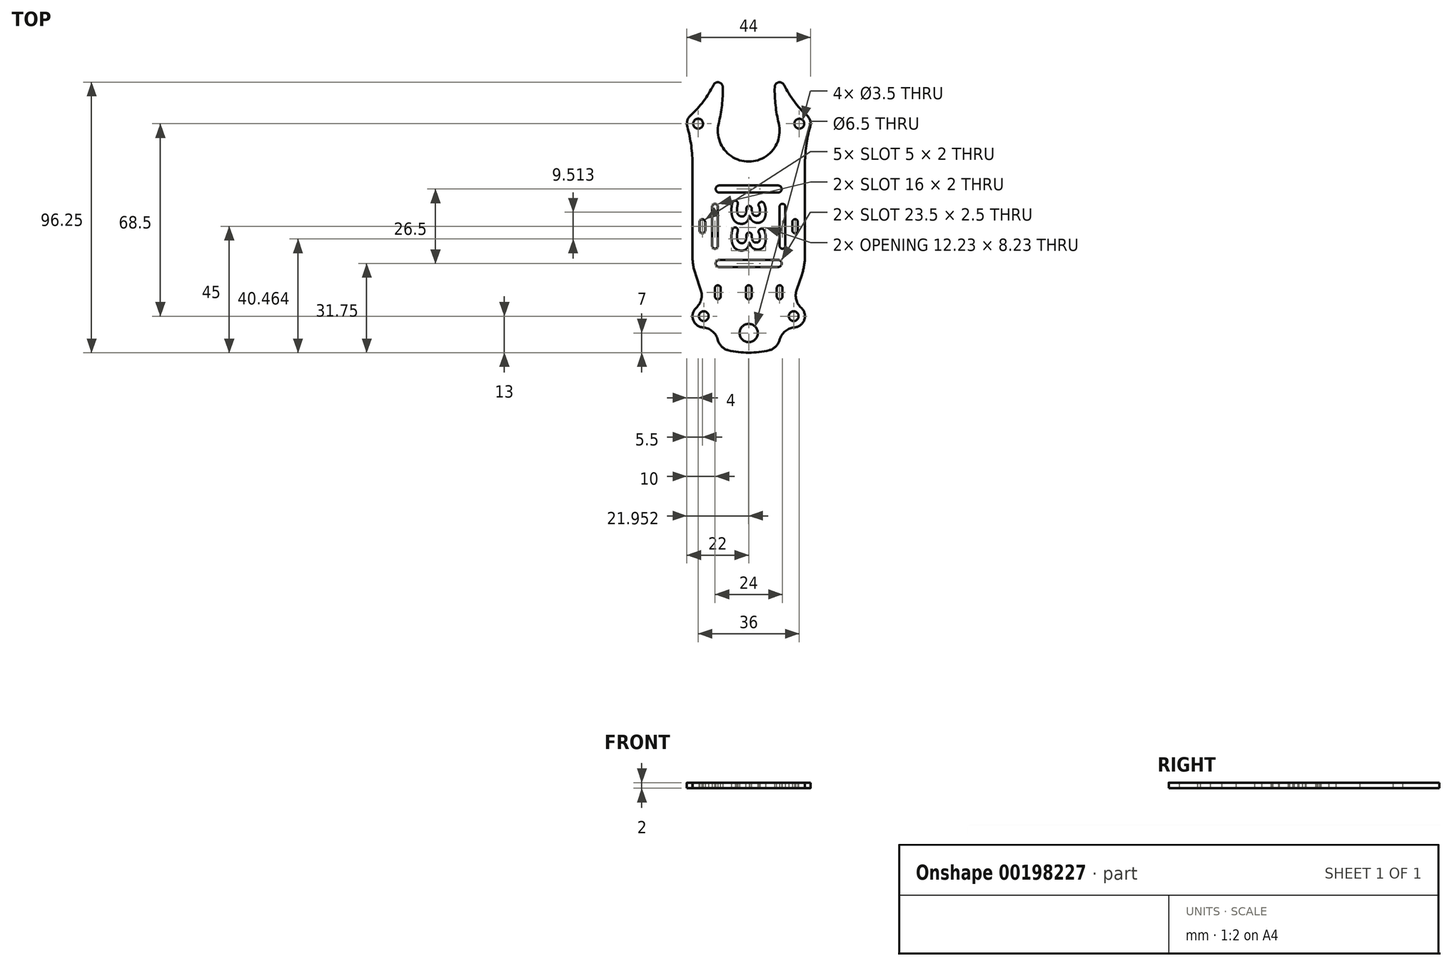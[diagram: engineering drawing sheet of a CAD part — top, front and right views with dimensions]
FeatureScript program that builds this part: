
annotation { "Feature Type Name" : "Feature", "Feature Type Description" : "" }
export const myFeature = defineFeature(function(context is Context, id is Id, definition is map)
    precondition{}
    {
        {
            var Q0;
            Q0=qCreatedBy(makeId("Top.planeOp"),FACE);
            var sketch = newSketch(context, id + "F0", { "sketchPlane" : qUnion([Q0])});
            skArc(sketch, "E0", {"start": v(-20.7, 39.46) * mm, "mid": v(-21.84, 37.62) * mm, "end": v(-21.86, 35.44) * mm});
            skLineSegment(sketch, "E1", {"start": v(-18.93, -17.14) * mm, "end": v(-17.05, -22.66) * mm});
            skArc(sketch, "E2", {"start": v(-10.68, 36.62) * mm, "mid": v(-8.66, 27.21) * mm, "end": v(0, 23) * mm});
            skLineSegment(sketch, "E3", {"start": v(0, 23) * mm, "end": v(0, -60) * mm, "construction": true});
            skCircle(sketch, "E4", {"center": v(-16, -32) * mm, "radius": 1.75 * mm});
            skArc(sketch, "E5.MirrorCS", {"start": v(10.68, 36.62) * mm, "mid": v(8.66, 27.21) * mm, "end": v(0, 23) * mm});
            skArc(sketch, "E6.MirrorCS", {"start": v(20.7, 39.46) * mm, "mid": v(21.84, 37.62) * mm, "end": v(21.86, 35.44) * mm});
            skCircle(sketch, "E7.MirrorC", {"center": v(16, -32) * mm, "radius": 1.75 * mm});
            skLineSegment(sketch, "E8.MirrorCS", {"start": v(18.93, -17.14) * mm, "end": v(17.05, -22.66) * mm});
            skCircle(sketch, "E9", {"center": v(-18, 36.5) * mm, "radius": 1.75 * mm});
            skCircle(sketch, "E10.MirrorC", {"center": v(18, 36.5) * mm, "radius": 1.75 * mm});
            skCircle(sketch, "E11", {"center": v(0, -38) * mm, "radius": 3.25 * mm});
            skArc(sketch, "E12", {"start": v(-7.28, -44.13) * mm, "mid": v(-3.66, -44.78) * mm, "end": v(0, -45) * mm});
            skLineSegment(sketch, "E13.trimOffspring", {"start": v(-20, 21.67) * mm, "end": v(-20, -10.69) * mm});
            skArc(sketch, "E14", {"start": v(16.32, -35.99) * mm, "mid": v(19.79, -33.3) * mm, "end": v(18.7, -29.04) * mm});
            skArc(sketch, "E15.filletArc", {"start": v(16.32, -35.99) * mm, "mid": v(13.12, -37.23) * mm, "end": v(11.13, -40.03) * mm});
            skArc(sketch, "E16.filletArc", {"start": v(17.05, -22.66) * mm, "mid": v(16.92, -26.1) * mm, "end": v(18.7, -29.04) * mm});
            skArc(sketch, "E17.MirrorCS", {"start": v(-16.32, -35.99) * mm, "mid": v(-13.12, -37.23) * mm, "end": v(-11.13, -40.03) * mm});
            skArc(sketch, "E18.MirrorCS", {"start": v(-16.32, -35.99) * mm, "mid": v(-19.79, -33.3) * mm, "end": v(-18.7, -29.04) * mm});
            skArc(sketch, "E19.MirrorCS", {"start": v(-17.05, -22.66) * mm, "mid": v(-16.92, -26.1) * mm, "end": v(-18.7, -29.04) * mm});
            skText(sketch, "E20", { "text": "33", "fontName": "OpenSans-Bold.ttf"});
            skLineSegment(sketch, "E21", {"start": v(-11.13, -40.03) * mm, "end": v(-10.84, -40.89) * mm});
            skLineSegment(sketch, "E22", {"start": v(11.13, -40.03) * mm, "end": v(10.84, -40.89) * mm});
            skLineSegment(sketch, "E23", {"start": v(-17.05, -22.66) * mm, "end": v(-11.13, -40.03) * mm, "construction": true});
            skLineSegment(sketch, "E24", {"start": v(17.05, -22.66) * mm, "end": v(11.13, -40.03) * mm, "construction": true});
            skArc(sketch, "E25", {"start": v(-9.25, 49.53) * mm, "mid": v(-10.62, 51.2) * mm, "end": v(-12.57, 50.27) * mm});
            skArc(sketch, "E26", {"start": v(-20.7, 39.46) * mm, "mid": v(-16.12, 44.48) * mm, "end": v(-12.57, 50.27) * mm});
            skArc(sketch, "E27.MirrorCS", {"start": v(9.25, 49.53) * mm, "mid": v(10.62, 51.2) * mm, "end": v(12.57, 50.27) * mm});
            skArc(sketch, "E28.MirrorCS", {"start": v(20.7, 39.46) * mm, "mid": v(16.12, 44.48) * mm, "end": v(12.57, 50.27) * mm});
            skPoint(sketch, "E29.visualSharp", {"position": v(-10, -43.34) * mm});
            skArc(sketch, "E29.filletArc", {"start": v(-10.84, -40.89) * mm, "mid": v(-9.47, -42.97) * mm, "end": v(-7.28, -44.13) * mm});
            skPoint(sketch, "E30.visualSharp", {"position": v(10, -43.34) * mm});
            skArc(sketch, "E30.filletArc", {"start": v(7.28, -44.13) * mm, "mid": v(9.47, -42.97) * mm, "end": v(10.84, -40.89) * mm});
            skLineSegment(sketch, "E31", {"start": v(-16.5, 1.5) * mm, "end": v(-16.5, -1.5) * mm, "construction": true});
            skArc(sketch, "E32.0.startCap", {"start": v(-17.5, 1.5) * mm, "mid": v(-16.5, 2.5) * mm, "end": v(-15.5, 1.5) * mm});
            skArc(sketch, "E32.0.endCap", {"start": v(-15.5, -1.5) * mm, "mid": v(-16.5, -2.5) * mm, "end": v(-17.5, -1.5) * mm});
            skLineSegment(sketch, "E32.0.left", {"start": v(-15.5, 1.5) * mm, "end": v(-15.5, -1.5) * mm});
            skLineSegment(sketch, "E32.0.right", {"start": v(-17.5, 1.5) * mm, "end": v(-17.5, -1.5) * mm});
            skLineSegment(sketch, "E33.MirrorCS", {"start": v(16.5, 1.5) * mm, "end": v(16.5, -1.5) * mm, "construction": true});
            skLineSegment(sketch, "E34.MirrorCS", {"start": v(15.5, 1.5) * mm, "end": v(15.5, -1.5) * mm});
            skLineSegment(sketch, "E35.MirrorCS", {"start": v(17.5, 1.5) * mm, "end": v(17.5, -1.5) * mm});
            skArc(sketch, "E36.MirrorCS", {"start": v(17.5, 1.5) * mm, "mid": v(16.5, 2.5) * mm, "end": v(15.5, 1.5) * mm});
            skArc(sketch, "E37.MirrorCS", {"start": v(15.5, -1.5) * mm, "mid": v(16.5, -2.5) * mm, "end": v(17.5, -1.5) * mm});
            skArc(sketch, "E38.filletArc", {"start": v(-10.68, 36.62) * mm, "mid": v(-9.55, 43.03) * mm, "end": v(-9.25, 49.53) * mm});
            skArc(sketch, "E39.filletArc", {"start": v(9.25, 49.53) * mm, "mid": v(9.55, 43.03) * mm, "end": v(10.68, 36.62) * mm});
            skArc(sketch, "E40", {"start": v(-20, 21.67) * mm, "mid": v(-20.47, 28.62) * mm, "end": v(-21.86, 35.44) * mm});
            skArc(sketch, "E41.MirrorCS", {"start": v(20, 21.67) * mm, "mid": v(20.47, 28.62) * mm, "end": v(21.86, 35.44) * mm});
            skCircle(sketch, "E42", {"center": v(0, -38) * mm, "radius": 4.5 * mm, "construction": true});
            skLineSegment(sketch, "E43", {"start": v(20, 21.67) * mm, "end": v(20, -10.69) * mm});
            skLineSegment(sketch, "E44", {"start": v(-10.5, 13.25) * mm, "end": v(10.5, 13.25) * mm, "construction": true});
            skLineSegment(sketch, "E45", {"start": v(-10.5, -13.25) * mm, "end": v(10.5, -13.25) * mm, "construction": true});
            skArc(sketch, "E46.0.startCap", {"start": v(-10.5, 12) * mm, "mid": v(-11.75, 13.25) * mm, "end": v(-10.5, 14.5) * mm});
            skArc(sketch, "E46.0.endCap", {"start": v(10.5, 14.5) * mm, "mid": v(11.75, 13.25) * mm, "end": v(10.5, 12) * mm});
            skLineSegment(sketch, "E46.0.left", {"start": v(-10.5, 14.5) * mm, "end": v(10.5, 14.5) * mm});
            skLineSegment(sketch, "E46.0.right", {"start": v(-10.5, 12) * mm, "end": v(10.5, 12) * mm});
            skArc(sketch, "E46.1.startCap", {"start": v(-10.5, -14.5) * mm, "mid": v(-11.75, -13.25) * mm, "end": v(-10.5, -12) * mm});
            skArc(sketch, "E46.1.endCap", {"start": v(10.5, -12) * mm, "mid": v(11.75, -13.25) * mm, "end": v(10.5, -14.5) * mm});
            skLineSegment(sketch, "E46.1.left", {"start": v(-10.5, -12) * mm, "end": v(10.5, -12) * mm});
            skLineSegment(sketch, "E46.1.right", {"start": v(-10.5, -14.5) * mm, "end": v(10.5, -14.5) * mm});
            skPoint(sketch, "E47.visualSharp", {"position": v(-20, -14) * mm});
            skArc(sketch, "E47.filletArc", {"start": v(-20, -10.69) * mm, "mid": v(-19.73, -13.96) * mm, "end": v(-18.93, -17.14) * mm});
            skPoint(sketch, "E48.visualSharp", {"position": v(20, -14) * mm});
            skArc(sketch, "E48.filletArc", {"start": v(18.93, -17.14) * mm, "mid": v(19.73, -13.96) * mm, "end": v(20, -10.69) * mm});
            skLineSegment(sketch, "E49", {"start": v(-12, 7) * mm, "end": v(-12, -7) * mm, "construction": true});
            skLineSegment(sketch, "E50.MirrorCS", {"start": v(12, 7) * mm, "end": v(12, -7) * mm, "construction": true});
            skArc(sketch, "E51.0.startCap", {"start": v(-13, 7) * mm, "mid": v(-12, 8) * mm, "end": v(-11, 7) * mm});
            skArc(sketch, "E51.0.endCap", {"start": v(-11, -7) * mm, "mid": v(-12, -8) * mm, "end": v(-13, -7) * mm});
            skLineSegment(sketch, "E51.0.left", {"start": v(-11, 7) * mm, "end": v(-11, -7) * mm});
            skLineSegment(sketch, "E51.0.right", {"start": v(-13, 7) * mm, "end": v(-13, -7) * mm});
            skArc(sketch, "E51.3.startCap", {"start": v(11, 7) * mm, "mid": v(12, 8) * mm, "end": v(13, 7) * mm});
            skArc(sketch, "E51.3.endCap", {"start": v(13, -7) * mm, "mid": v(12, -8) * mm, "end": v(11, -7) * mm});
            skLineSegment(sketch, "E51.3.left", {"start": v(13, 7) * mm, "end": v(13, -7) * mm});
            skLineSegment(sketch, "E51.3.right", {"start": v(11, 7) * mm, "end": v(11, -7) * mm});
            skPoint(sketch, "E52.startSnap0", {"position": v(-16.5, 2.5) * mm});
            skArc(sketch, "E53.trimOffspring", {"start": v(0, -45) * mm, "mid": v(3.66, -44.78) * mm, "end": v(7.28, -44.13) * mm});
            const initialGuessF0  = {"E20": [-0.006, 0.00973, 0, -1, 0.012]};
            skSetInitialGuess(sketch, initialGuessF0);
            skSolve(sketch);
        }
        {
            var Q0;
            Q0=qSketchRegion(id+"F0",true);
            extrude(context, id + "F1", {"entities" : qUnion([Q0]), "depth" : 2 * mm});
        }
        {
            var Q0;
            Q0=makeQuery(id+"F1.opExtrude","SWEPT_EDGE",EDGE,{"disambiguationData":[OSD([sQuery(id+"F0.wireOp",EDGE,"E20.sketch_text.stroke-23"),sQuery(id+"F0.wireOp",EDGE,"E20.sketch_text.stroke-24")])]});
            var Q1;
            Q1=makeQuery(id+"F1.opExtrude","SWEPT_EDGE",EDGE,{"disambiguationData":[OSD([sQuery(id+"F0.wireOp",EDGE,"E20.sketch_text.stroke-22"),sQuery(id+"F0.wireOp",EDGE,"E20.sketch_text.stroke-23")])]});
            var Q2;
            Q2=makeQuery(id+"F1.opExtrude","SWEPT_EDGE",EDGE,{"disambiguationData":[OSD([sQuery(id+"F0.wireOp",EDGE,"E20.sketch_text.stroke-16"),sQuery(id+"F0.wireOp",EDGE,"E20.sketch_text.stroke-17")])]});
            var Q3;
            Q3=makeQuery(id+"F1.opExtrude","SWEPT_EDGE",EDGE,{"disambiguationData":[OSD([sQuery(id+"F0.wireOp",EDGE,"E20.sketch_text.stroke-15"),sQuery(id+"F0.wireOp",EDGE,"E20.sketch_text.stroke-16")])]});
            var Q4;
            Q4=makeQuery(id+"F1.opExtrude","SWEPT_EDGE",EDGE,{"disambiguationData":[OSD([sQuery(id+"F0.wireOp",EDGE,"E20.sketch_text.stroke-8"),sQuery(id+"F0.wireOp",EDGE,"E20.sketch_text.stroke-9")])]});
            var Q5;
            Q5=makeQuery(id+"F1.opExtrude","SWEPT_EDGE",EDGE,{"disambiguationData":[OSD([sQuery(id+"F0.wireOp",EDGE,"E20.sketch_text.stroke-7"),sQuery(id+"F0.wireOp",EDGE,"E20.sketch_text.stroke-8")])]});
            var Q6;
            Q6=makeQuery(id+"F1.opExtrude","SWEPT_EDGE",EDGE,{"disambiguationData":[OSD([sQuery(id+"F0.wireOp",EDGE,"E20.sketch_text.stroke-35"),sQuery(id+"F0.wireOp",EDGE,"E20.sketch_text.stroke-36")])]});
            var Q7;
            Q7=makeQuery(id+"F1.opExtrude","SWEPT_EDGE",EDGE,{"disambiguationData":[OSD([sQuery(id+"F0.wireOp",EDGE,"E20.sketch_text.stroke-34"),sQuery(id+"F0.wireOp",EDGE,"E20.sketch_text.stroke-35")])]});
            var Q8;
            Q8=makeQuery(id+"F1.opExtrude","SWEPT_EDGE",EDGE,{"disambiguationData":[OSD([sQuery(id+"F0.wireOp",EDGE,"E20.sketch_text.stroke-42"),sQuery(id+"F0.wireOp",EDGE,"E20.sketch_text.stroke-43")])]});
            var Q9;
            Q9=makeQuery(id+"F1.opExtrude","SWEPT_EDGE",EDGE,{"disambiguationData":[OSD([sQuery(id+"F0.wireOp",EDGE,"E20.sketch_text.stroke-43"),sQuery(id+"F0.wireOp",EDGE,"E20.sketch_text.stroke-44")])]});
            var Q10;
            Q10=makeQuery(id+"F1.opExtrude","SWEPT_EDGE",EDGE,{"disambiguationData":[OSD([sQuery(id+"F0.wireOp",EDGE,"E20.sketch_text.stroke-49"),sQuery(id+"F0.wireOp",EDGE,"E20.sketch_text.stroke-50")])]});
            var Q11;
            Q11=makeQuery(id+"F1.opExtrude","SWEPT_EDGE",EDGE,{"disambiguationData":[OSD([sQuery(id+"F0.wireOp",EDGE,"E20.sketch_text.stroke-50"),sQuery(id+"F0.wireOp",EDGE,"E20.sketch_text.stroke-51")])]});
            fillet(context, id + "F2", {"entities" : qUnion([Q0, Q1, Q2, Q3, Q4, Q5, Q6, Q7, Q8, Q9, Q10, Q11]), "radius" : 1 * mm, "tangentPropagation" : true, "allowEdgeOverflow" : false});
        }
        {
            var Q0;
            Q0=makeQuery(id+"F1.opExtrude","CAP_FACE",FACE,{"disambiguationData":[OSD([sQuery(id+"F0.wireOp",EDGE,"E0"),sQuery(id+"F0.wireOp",EDGE,"E1"),sQuery(id+"F0.wireOp",EDGE,"E2"),sQuery(id+"F0.wireOp",EDGE,"E4"),sQuery(id+"F0.wireOp",EDGE,"E5.MirrorCS"),sQuery(id+"F0.wireOp",EDGE,"E6.MirrorCS"),sQuery(id+"F0.wireOp",EDGE,"E7.MirrorC"),sQuery(id+"F0.wireOp",EDGE,"E8.MirrorCS"),sQuery(id+"F0.wireOp",EDGE,"E9"),sQuery(id+"F0.wireOp",EDGE,"E10.MirrorC"),sQuery(id+"F0.wireOp",EDGE,"E11"),sQuery(id+"F0.wireOp",EDGE,"E12"),sQuery(id+"F0.wireOp",EDGE,"E13.trimOffspring"),sQuery(id+"F0.wireOp",EDGE,"E14"),sQuery(id+"F0.wireOp",EDGE,"E15.filletArc"),sQuery(id+"F0.wireOp",EDGE,"E16.filletArc"),sQuery(id+"F0.wireOp",EDGE,"E17.MirrorCS"),sQuery(id+"F0.wireOp",EDGE,"E18.MirrorCS"),sQuery(id+"F0.wireOp",EDGE,"E19.MirrorCS"),sQuery(id+"F0.wireOp",EDGE,"E20.sketch_text.stroke-0"),sQuery(id+"F0.wireOp",EDGE,"E20.sketch_text.stroke-1"),sQuery(id+"F0.wireOp",EDGE,"E20.sketch_text.stroke-2"),sQuery(id+"F0.wireOp",EDGE,"E20.sketch_text.stroke-3"),sQuery(id+"F0.wireOp",EDGE,"E20.sketch_text.stroke-4"),sQuery(id+"F0.wireOp",EDGE,"E20.sketch_text.stroke-5"),sQuery(id+"F0.wireOp",EDGE,"E20.sketch_text.stroke-6"),sQuery(id+"F0.wireOp",EDGE,"E20.sketch_text.stroke-7"),sQuery(id+"F0.wireOp",EDGE,"E20.sketch_text.stroke-8"),sQuery(id+"F0.wireOp",EDGE,"E20.sketch_text.stroke-9"),sQuery(id+"F0.wireOp",EDGE,"E20.sketch_text.stroke-10"),sQuery(id+"F0.wireOp",EDGE,"E20.sketch_text.stroke-11"),sQuery(id+"F0.wireOp",EDGE,"E20.sketch_text.stroke-12"),sQuery(id+"F0.wireOp",EDGE,"E20.sketch_text.stroke-13"),sQuery(id+"F0.wireOp",EDGE,"E20.sketch_text.stroke-14"),sQuery(id+"F0.wireOp",EDGE,"E20.sketch_text.stroke-15"),sQuery(id+"F0.wireOp",EDGE,"E20.sketch_text.stroke-16"),sQuery(id+"F0.wireOp",EDGE,"E20.sketch_text.stroke-17"),sQuery(id+"F0.wireOp",EDGE,"E20.sketch_text.stroke-18"),sQuery(id+"F0.wireOp",EDGE,"E20.sketch_text.stroke-19"),sQuery(id+"F0.wireOp",EDGE,"E20.sketch_text.stroke-20"),sQuery(id+"F0.wireOp",EDGE,"E20.sketch_text.stroke-21"),sQuery(id+"F0.wireOp",EDGE,"E20.sketch_text.stroke-22"),sQuery(id+"F0.wireOp",EDGE,"E20.sketch_text.stroke-23"),sQuery(id+"F0.wireOp",EDGE,"E20.sketch_text.stroke-24"),sQuery(id+"F0.wireOp",EDGE,"E20.sketch_text.stroke-25"),sQuery(id+"F0.wireOp",EDGE,"E20.sketch_text.stroke-26"),sQuery(id+"F0.wireOp",EDGE,"E20.sketch_text.stroke-27"),sQuery(id+"F0.wireOp",EDGE,"E20.sketch_text.stroke-28"),sQuery(id+"F0.wireOp",EDGE,"E20.sketch_text.stroke-29"),sQuery(id+"F0.wireOp",EDGE,"E20.sketch_text.stroke-30"),sQuery(id+"F0.wireOp",EDGE,"E20.sketch_text.stroke-31"),sQuery(id+"F0.wireOp",EDGE,"E20.sketch_text.stroke-32"),sQuery(id+"F0.wireOp",EDGE,"E20.sketch_text.stroke-33"),sQuery(id+"F0.wireOp",EDGE,"E20.sketch_text.stroke-34"),sQuery(id+"F0.wireOp",EDGE,"E20.sketch_text.stroke-35"),sQuery(id+"F0.wireOp",EDGE,"E20.sketch_text.stroke-36"),sQuery(id+"F0.wireOp",EDGE,"E20.sketch_text.stroke-37"),sQuery(id+"F0.wireOp",EDGE,"E20.sketch_text.stroke-38"),sQuery(id+"F0.wireOp",EDGE,"E20.sketch_text.stroke-39"),sQuery(id+"F0.wireOp",EDGE,"E20.sketch_text.stroke-40"),sQuery(id+"F0.wireOp",EDGE,"E20.sketch_text.stroke-41"),sQuery(id+"F0.wireOp",EDGE,"E20.sketch_text.stroke-42"),sQuery(id+"F0.wireOp",EDGE,"E20.sketch_text.stroke-43"),sQuery(id+"F0.wireOp",EDGE,"E20.sketch_text.stroke-44"),sQuery(id+"F0.wireOp",EDGE,"E20.sketch_text.stroke-45"),sQuery(id+"F0.wireOp",EDGE,"E20.sketch_text.stroke-46"),sQuery(id+"F0.wireOp",EDGE,"E20.sketch_text.stroke-47"),sQuery(id+"F0.wireOp",EDGE,"E20.sketch_text.stroke-48"),sQuery(id+"F0.wireOp",EDGE,"E20.sketch_text.stroke-49"),sQuery(id+"F0.wireOp",EDGE,"E20.sketch_text.stroke-50"),sQuery(id+"F0.wireOp",EDGE,"E20.sketch_text.stroke-51"),sQuery(id+"F0.wireOp",EDGE,"E20.sketch_text.stroke-52"),sQuery(id+"F0.wireOp",EDGE,"E20.sketch_text.stroke-53"),sQuery(id+"F0.wireOp",EDGE,"E21"),sQuery(id+"F0.wireOp",EDGE,"E22"),sQuery(id+"F0.wireOp",EDGE,"E25"),sQuery(id+"F0.wireOp",EDGE,"E26"),sQuery(id+"F0.wireOp",EDGE,"E27.MirrorCS"),sQuery(id+"F0.wireOp",EDGE,"E28.MirrorCS"),sQuery(id+"F0.wireOp",EDGE,"E29.filletArc"),sQuery(id+"F0.wireOp",EDGE,"E30.filletArc"),sQuery(id+"F0.wireOp",EDGE,"E32.0.startCap"),sQuery(id+"F0.wireOp",EDGE,"E32.0.endCap"),sQuery(id+"F0.wireOp",EDGE,"E32.0.left"),sQuery(id+"F0.wireOp",EDGE,"E32.0.right"),sQuery(id+"F0.wireOp",EDGE,"E34.MirrorCS"),sQuery(id+"F0.wireOp",EDGE,"E35.MirrorCS"),sQuery(id+"F0.wireOp",EDGE,"E36.MirrorCS"),sQuery(id+"F0.wireOp",EDGE,"E37.MirrorCS"),sQuery(id+"F0.wireOp",EDGE,"E38.filletArc"),sQuery(id+"F0.wireOp",EDGE,"E39.filletArc"),sQuery(id+"F0.wireOp",EDGE,"E40"),sQuery(id+"F0.wireOp",EDGE,"E41.MirrorCS"),sQuery(id+"F0.wireOp",EDGE,"E43"),sQuery(id+"F0.wireOp",EDGE,"E46.0.startCap"),sQuery(id+"F0.wireOp",EDGE,"E46.0.endCap"),sQuery(id+"F0.wireOp",EDGE,"E46.0.left"),sQuery(id+"F0.wireOp",EDGE,"E46.0.right"),sQuery(id+"F0.wireOp",EDGE,"E46.1.startCap"),sQuery(id+"F0.wireOp",EDGE,"E46.1.endCap"),sQuery(id+"F0.wireOp",EDGE,"E46.1.left"),sQuery(id+"F0.wireOp",EDGE,"E46.1.right"),sQuery(id+"F0.wireOp",EDGE,"E47.filletArc"),sQuery(id+"F0.wireOp",EDGE,"E48.filletArc"),sQuery(id+"F0.wireOp",EDGE,"E51.0.startCap"),sQuery(id+"F0.wireOp",EDGE,"E51.0.endCap"),sQuery(id+"F0.wireOp",EDGE,"E51.0.left"),sQuery(id+"F0.wireOp",EDGE,"E51.0.right"),sQuery(id+"F0.wireOp",EDGE,"E51.3.startCap"),sQuery(id+"F0.wireOp",EDGE,"E51.3.endCap"),sQuery(id+"F0.wireOp",EDGE,"E51.3.left"),sQuery(id+"F0.wireOp",EDGE,"E51.3.right"),sQuery(id+"F0.wireOp",EDGE,"E53.trimOffspring")])],"isStart":false});
            var sketch = newSketch(context, id + "F3", { "sketchPlane" : qUnion([Q0])});
            skLineSegment(sketch, "E54", {"start": v(11, -22) * mm, "end": v(11, -25) * mm});
            skLineSegment(sketch, "E55", {"start": v(0, -22) * mm, "end": v(0, -25) * mm});
            skArc(sketch, "E56.0.startCap", {"start": v(10, -22) * mm, "mid": v(11, -21) * mm, "end": v(12, -22) * mm});
            skArc(sketch, "E56.0.endCap", {"start": v(12, -25) * mm, "mid": v(11, -26) * mm, "end": v(10, -25) * mm});
            skLineSegment(sketch, "E56.0.left", {"start": v(12, -22) * mm, "end": v(12, -25) * mm});
            skLineSegment(sketch, "E56.0.right", {"start": v(10, -22) * mm, "end": v(10, -25) * mm});
            skArc(sketch, "E56.1.startCap", {"start": v(-1, -22) * mm, "mid": v(0, -21) * mm, "end": v(1, -22) * mm});
            skArc(sketch, "E56.1.endCap", {"start": v(1, -25) * mm, "mid": v(0, -26) * mm, "end": v(-1, -25) * mm});
            skLineSegment(sketch, "E56.1.left", {"start": v(1, -22) * mm, "end": v(1, -25) * mm});
            skLineSegment(sketch, "E56.1.right", {"start": v(-1, -22) * mm, "end": v(-1, -25) * mm});
            skLineSegment(sketch, "E57.MirrorCS", {"start": v(-10, -22) * mm, "end": v(-10, -25) * mm});
            skLineSegment(sketch, "E58.MirrorCS", {"start": v(-12, -22) * mm, "end": v(-12, -25) * mm});
            skLineSegment(sketch, "E59.MirrorCS", {"start": v(-11, -22) * mm, "end": v(-11, -25) * mm});
            skArc(sketch, "E60.MirrorCS", {"start": v(-10, -22) * mm, "mid": v(-11, -21) * mm, "end": v(-12, -22) * mm});
            skArc(sketch, "E61.MirrorCS", {"start": v(-12, -25) * mm, "mid": v(-11, -26) * mm, "end": v(-10, -25) * mm});
            skSolve(sketch);
        }
        {
            var Q0;
            Q0 = qSketchRegion(id + "F3", true);
            extrude(context, id + "F4", {"entities" : qUnion([Q0]), "operationType" : NewBodyOperationType.REMOVE, "oppositeDirection" : true, "depth" : 25 * mm});
        }
    });
